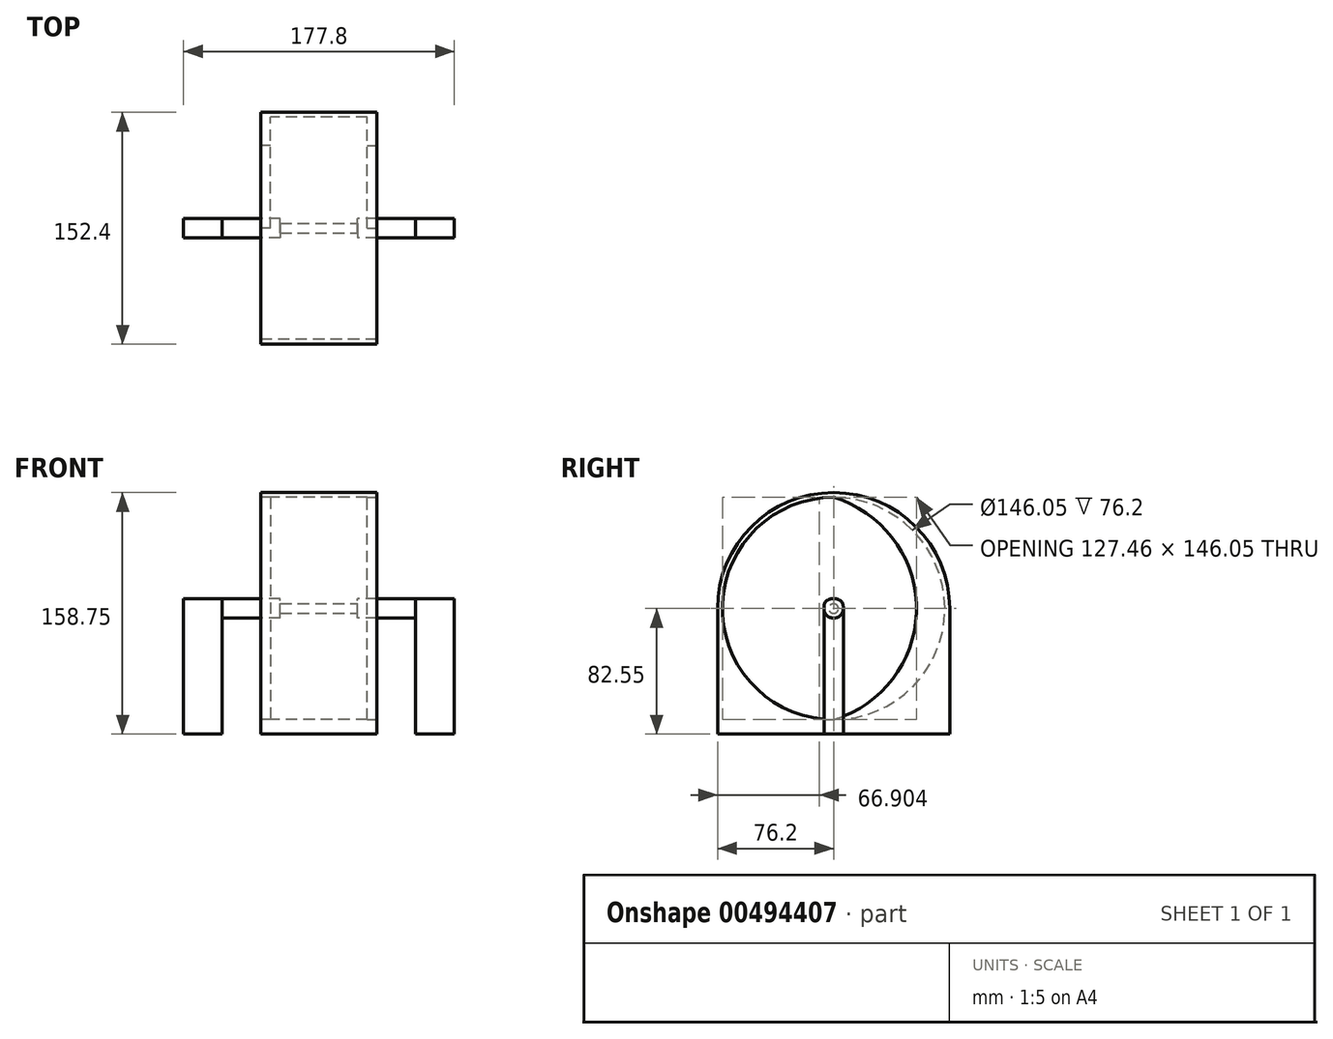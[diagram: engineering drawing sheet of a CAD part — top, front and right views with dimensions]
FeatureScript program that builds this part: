
annotation { "Feature Type Name" : "Feature", "Feature Type Description" : "" }
export const myFeature = defineFeature(function(context is Context, id is Id, definition is map)
    precondition{}
    {
        {
            var Q0;
            Q0=qCreatedBy(makeId("Right.planeOp"),FACE);
            var sketch = newSketch(context, id + "F0", { "sketchPlane" : qUnion([Q0])});
            skCircle(sketch, "E0", {"center": v(0, 0) * mm, "radius": 76.2 * mm});
            skCircle(sketch, "E1", {"center": v(0, 0) * mm, "radius": 73.03 * mm});
            skLineSegment(sketch, "E2", {"start": v(76.2, 0) * mm, "end": v(76.2, -82.55) * mm});
            skLineSegment(sketch, "E3", {"start": v(-76.2, 0) * mm, "end": v(-76.2, -82.55) * mm});
            skLineSegment(sketch, "E4", {"start": v(76.2, -82.55) * mm, "end": v(-76.2, -82.55) * mm});
            skSolve(sketch);
        }
        {
            var Q0;
            Q0=makeQuery(id+"F0.imprint","IMPRINT",FACE,{"disambiguationData":[TD([[makeQuery(id+"F0.imprint","IMPRINT",EDGE,{"derivedFrom":sQuery(id+"F0.wireOp",EDGE,"E0")}),1.0]])]});
            extrude(context, id + "F1", {"entities" : qUnion([Q0]), "depth" : 76.2 * mm});
        }
        {
            var Q0;
            Q0=makeQuery(id+"F1.opExtrude","CAP_FACE",FACE,{"disambiguationData":[OSD([sQuery(id+"F0.wireOp",EDGE,"E0"),sQuery(id+"F0.wireOp",EDGE,"E1")])],"isStart":false});
            cPlane(context, id + "F2", {"entities" : qUnion([Q0]), "cplaneType" : CPlaneType.OFFSET, "offset" : 0 * mm, "width" : 152.4 * mm, "height" : 152.4 * mm});
        }
        {
            var Q0;
            Q0=qCreatedBy(id+"F2.planeOp",FACE);
            var sketch = newSketch(context, id + "F3", { "sketchPlane" : qUnion([Q0])});
            skArc(sketch, "E5", {"start": v(0, -73.03) * mm, "mid": v(54.43, 0) * mm, "end": v(0, 73.03) * mm});
            skArc(sketch, "E6", {"start": v(0, -73.03) * mm, "mid": v(73.03, 0) * mm, "end": v(0, 73.03) * mm});
            skSolve(sketch);
        }
        {
            var Q0;
            Q0=makeQuery(id+"F3.imprint","IMPRINT",FACE,{"disambiguationData":[TD([[makeQuery(id+"F3.imprint","IMPRINT",EDGE,{"derivedFrom":sQuery(id+"F3.wireOp",EDGE,"E5")}),-1.0]])]});
            extrude(context, id + "F4", {"entities" : qUnion([Q0]), "operationType" : NewBodyOperationType.ADD, "oppositeDirection" : true, "depth" : 6.35 * mm});
        }
        {
            var Q0;
            Q0=makeQuery(id+"F1.opExtrude","CAP_FACE",FACE,{"disambiguationData":[OSD([sQuery(id+"F0.wireOp",EDGE,"E0"),sQuery(id+"F0.wireOp",EDGE,"E1")])],"isStart":true});
            cPlane(context, id + "F5", {"entities" : qUnion([Q0]), "cplaneType" : CPlaneType.OFFSET, "offset" : 0 * mm, "width" : 152.4 * mm, "height" : 152.4 * mm});
        }
        {
            var Q0;
            Q0=qCreatedBy(id+"F5.planeOp",FACE);
            var sketch = newSketch(context, id + "F6", { "sketchPlane" : qUnion([Q0])});
            skArc(sketch, "E7", {"start": v(0, 73.02) * mm, "mid": v(-54.43, 0) * mm, "end": v(0, -73.03) * mm});
            skArc(sketch, "E8", {"start": v(0, 73.03) * mm, "mid": v(-73.03, 0) * mm, "end": v(0, -73.03) * mm});
            skSolve(sketch);
        }
        {
            var Q0;
            Q0=makeQuery(id+"F6.imprint","IMPRINT",FACE,{"disambiguationData":[TD([[makeQuery(id+"F6.imprint","IMPRINT",EDGE,{"derivedFrom":sQuery(id+"F6.wireOp",EDGE,"E7")}),-1.0]])]});
            extrude(context, id + "F7", {"entities" : qUnion([Q0]), "operationType" : NewBodyOperationType.ADD, "oppositeDirection" : true, "depth" : 6.35 * mm});
        }
        {
            var Q0;
            Q0=qCreatedBy(id+"F2.planeOp",FACE);
            cPlane(context, id + "F8", {"entities" : qUnion([Q0]), "cplaneType" : CPlaneType.OFFSET, "offset" : 38.1 * mm, "oppositeDirection" : true, "width" : 152.4 * mm, "height" : 152.4 * mm});
        }
        {
            var Q0;
            Q0=qCreatedBy(id+"F8.planeOp",FACE);
            var sketch = newSketch(context, id + "F9", { "sketchPlane" : qUnion([Q0])});
            skCircle(sketch, "E9", {"center": v(0, 0) * mm, "radius": 6.35 * mm});
            skSolve(sketch);
        }
        {
            var Q0;
            Q0=makeQuery(id+"F9.imprint","IMPRINT",FACE,{"disambiguationData":[TD([[makeQuery(id+"F9.imprint","IMPRINT",EDGE,{"derivedFrom":sQuery(id+"F9.wireOp",EDGE,"E9")}),1.0]])]});
            extrude(context, id + "F10", {"entities" : qUnion([Q0]), "depth" : 127 * mm, "symmetric" : true});
        }
        {
            var Q0;
            Q0=qCreatedBy(id+"F8.planeOp",FACE);
            var sketch = newSketch(context, id + "F11", { "sketchPlane" : qUnion([Q0])});
            skCircle(sketch, "E10", {"center": v(0, 0) * mm, "radius": 7.34 * mm});
            skCircle(sketch, "E11", {"center": v(0, 0) * mm, "radius": 3.17 * mm});
            skSolve(sketch);
        }
        {
            var Q0;
            Q0 = qSketchRegion(id + "F11", true);
            extrude(context, id + "F12", {"entities" : qUnion([Q0]), "operationType" : NewBodyOperationType.REMOVE, "oppositeDirection" : true, "depth" : 50.8 * mm, "symmetric" : true});
        }
        {
            var Q0;
            {var subQ0=sQuery(id+"F0.wireOp",EDGE,"E2");Q0=makeQuery(id+"F0.imprint","IMPRINT",FACE,{"disambiguationData":[TD([[makeQuery(id+"F0.imprint","IMPRINT",EDGE,{"derivedFrom":subQ0}),-1.0]])]});}
            extrude(context, id + "F13", {"entities" : qUnion([Q0]), "operationType" : NewBodyOperationType.ADD, "depth" : 76.2 * mm});
        }
        {
            var Q0;
            Q0=makeQuery(id+"F10.opExtrude","CAP_FACE",FACE,{"disambiguationData":[OSD([sQuery(id+"F9.wireOp",EDGE,"E9")])],"isStart":true});
            var sketch = newSketch(context, id + "F14", { "sketchPlane" : qUnion([Q0])});
            skLineSegment(sketch, "E12.bottom", {"start": v(-6.35, 6.35) * mm, "end": v(6.35, 6.35) * mm});
            skLineSegment(sketch, "E12.top", {"start": v(-6.35, -82.55) * mm, "end": v(6.35, -82.55) * mm});
            skLineSegment(sketch, "E12.left", {"start": v(-6.35, 6.35) * mm, "end": v(-6.35, -82.55) * mm});
            skLineSegment(sketch, "E12.right", {"start": v(6.35, 6.35) * mm, "end": v(6.35, -82.55) * mm});
            skSolve(sketch);
        }
        {
            var Q0;
            Q0 = qSketchRegion(id + "F14", true);
            extrude(context, id + "F15", {"entities" : qUnion([Q0]), "operationType" : NewBodyOperationType.ADD, "depth" : 25.4 * mm});
        }
        {
            var Q0;
            Q0=makeQuery(id+"F10.opExtrude","CAP_FACE",FACE,{"disambiguationData":[OSD([sQuery(id+"F9.wireOp",EDGE,"E9")])],"isStart":false});
            var sketch = newSketch(context, id + "F16", { "sketchPlane" : qUnion([Q0])});
            skLineSegment(sketch, "E13.bottom", {"start": v(-6.35, 6.35) * mm, "end": v(6.35, 6.35) * mm});
            skLineSegment(sketch, "E13.top", {"start": v(-6.35, -82.55) * mm, "end": v(6.35, -82.55) * mm});
            skLineSegment(sketch, "E13.left", {"start": v(-6.35, 6.35) * mm, "end": v(-6.35, -82.55) * mm});
            skLineSegment(sketch, "E13.right", {"start": v(6.35, 6.35) * mm, "end": v(6.35, -82.55) * mm});
            skPoint(sketch, "E14.startSnap0", {"position": v(0, 6.35) * mm});
            skSolve(sketch);
        }
        {
            var Q0;
            Q0 = qSketchRegion(id + "F16", true);
            extrude(context, id + "F17", {"entities" : qUnion([Q0]), "operationType" : NewBodyOperationType.ADD, "depth" : 25.4 * mm});
        }
        {
            var Q0;
            Q0=makeQuery(id+"F15.opExtrude","SWEPT_EDGE",EDGE,{"disambiguationData":[OSD([sQuery(id+"F14.wireOp",EDGE,"E12.bottom"),sQuery(id+"F14.wireOp",EDGE,"E12.left")])]});
            var Q1;
            Q1=makeQuery(id+"F15.opExtrude","SWEPT_EDGE",EDGE,{"disambiguationData":[OSD([sQuery(id+"F14.wireOp",EDGE,"E12.bottom"),sQuery(id+"F14.wireOp",EDGE,"E12.right")])]});
            var Q2;
            Q2=makeQuery(id+"F17.opExtrude","SWEPT_EDGE",EDGE,{"disambiguationData":[OSD([sQuery(id+"F16.wireOp",EDGE,"E13.bottom"),sQuery(id+"F16.wireOp",EDGE,"E13.left")])]});
            var Q3;
            Q3=makeQuery(id+"F17.opExtrude","SWEPT_EDGE",EDGE,{"disambiguationData":[OSD([sQuery(id+"F16.wireOp",EDGE,"E13.bottom"),sQuery(id+"F16.wireOp",EDGE,"E13.right")])]});
            fillet(context, id + "F18", {"entities" : qUnion([Q0, Q1, Q2, Q3]), "radius" : 5.08 * mm, "tangentPropagation" : true, "allowEdgeOverflow" : false});
        }
    });
